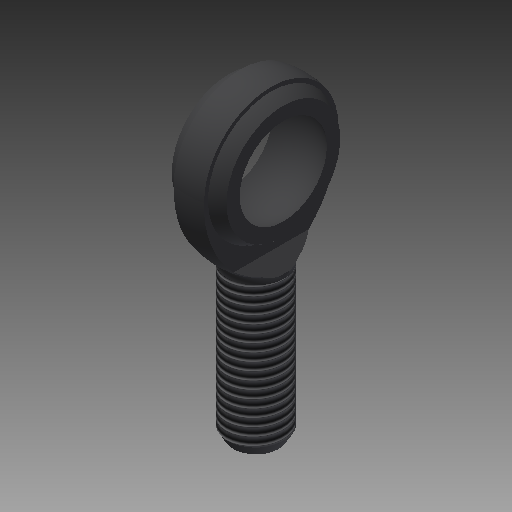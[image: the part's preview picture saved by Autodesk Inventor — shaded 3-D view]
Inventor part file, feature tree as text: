
AUTODESK INVENTOR PART (.ipt)
format: ipt  version: 2018 (Build 220112000, 112)  size: 208,384 bytes
history: native  units: mm
features: other x7, sketch x4, revolve x3, thread x1, extrude x1
ambient origin geometry x8: Origin, YZ Plane, XZ Plane, XY Plane, X Axis, Y Axis, Z Axis, Center Point
bodies: Solid1 (feature_tree)
feature tree (16):
  revolve  "Revolution1"  [1 undecoded]
  thread  "Thread1"  [1 undecoded]
  extrude  "Extrusion1"  TaperAngle=360.0deg  [1 undecoded]
  revolve  "Revolution2"  [1 undecoded]
  revolve  "Revolution3"  [1 undecoded]
  other  "IP_1_BO_XY"
  other  "IP_1_BO_YZ"
  other  "IP_1_BO_ZX"
  other  "IP_1_BO_X"
  other  "IP_1_BO_Y"
  other  "IP_1_BO_Z"
  other  "IP_1_BO_Center"
  sketch  "Sketch_4"  dims[d0=360.0deg d1=33.5751mm d2=0.0mm d3=34.0mm d4=0.0mm]
  sketch  "Sketch_5"  dims[d5=360.0deg d6=360.0deg]
  sketch  "Sketch_6"
  sketch  "Sketch_7"
note: 5 required parameter values undecoded (feature->parameter linkage not recoverable at this tier; creation-order binding heuristic only, values carry confidence <= 0.55)